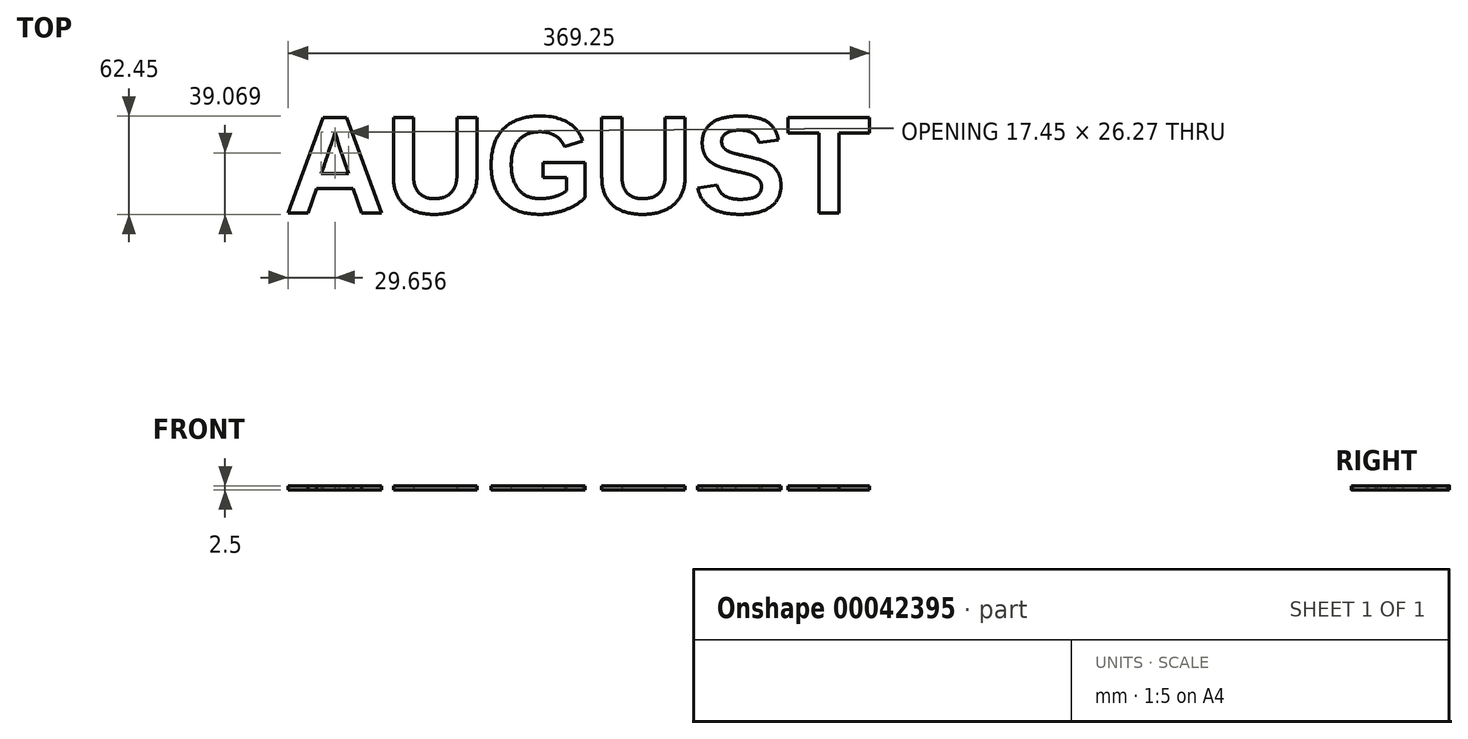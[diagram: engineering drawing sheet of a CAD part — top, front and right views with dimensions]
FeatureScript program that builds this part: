
annotation { "Feature Type Name" : "Feature", "Feature Type Description" : "" }
export const myFeature = defineFeature(function(context is Context, id is Id, definition is map)
    precondition{}
    {
        {
            assignVariable(context, id + "F0", {"name" : "x", "anyValue" : 2.5});
        }
        {
            var Q0;
            Q0=qCreatedBy(makeId("Top.planeOp"),FACE);
            var sketch = newSketch(context, id + "F1", { "sketchPlane" : qUnion([Q0])});
            skText(sketch, "E0", { "text": "AUGUST", "fontName": "Arimo-Bold.ttf"});
            skLineSegment(sketch, "E1.rect.bottom", {"start": v(222.25, -63.5) * mm, "end": v(-222.25, -63.5) * mm});
            skLineSegment(sketch, "E1.rect.top", {"start": v(222.25, 63.5) * mm, "end": v(-222.25, 63.5) * mm});
            skLineSegment(sketch, "E1.rect.left", {"start": v(222.25, -63.5) * mm, "end": v(222.25, 63.5) * mm});
            skLineSegment(sketch, "E1.rect.right", {"start": v(-222.25, -63.5) * mm, "end": v(-222.25, 63.5) * mm});
            skPoint(sketch, "E1.rect.middle", {"position": v(0, 0) * mm});
            const initialGuessF1  = {"E0": [-0.18572, -0.03175, 1, 0, 0.0635]};
            skSetInitialGuess(sketch, initialGuessF1);
            skSolve(sketch);
        }
        {
            var Q0;
            Q0=makeQuery(id+"F1.imprint","IMPRINT",FACE,{"disambiguationData":[TD([[makeQuery(id+"F1.imprint","IMPRINT",EDGE,{"derivedFrom":sQuery(id+"F1.wireOp",EDGE,"E0.sketch_text.stroke-0")}),-1.0]])]});
            var Q1;
            Q1=makeQuery(id+"F1.imprint","IMPRINT",FACE,{"disambiguationData":[TD([[makeQuery(id+"F1.imprint","IMPRINT",EDGE,{"derivedFrom":sQuery(id+"F1.wireOp",EDGE,"E0.sketch_text.stroke-15")}),-1.0]])]});
            var Q2;
            Q2=makeQuery(id+"F1.imprint","IMPRINT",FACE,{"disambiguationData":[TD([[makeQuery(id+"F1.imprint","IMPRINT",EDGE,{"derivedFrom":sQuery(id+"F1.wireOp",EDGE,"E0.sketch_text.stroke-29")}),-1.0]])]});
            var Q3;
            Q3=makeQuery(id+"F1.imprint","IMPRINT",FACE,{"disambiguationData":[TD([[makeQuery(id+"F1.imprint","IMPRINT",EDGE,{"derivedFrom":sQuery(id+"F1.wireOp",EDGE,"E0.sketch_text.stroke-50")}),-1.0]])]});
            var Q4;
            Q4=makeQuery(id+"F1.imprint","IMPRINT",FACE,{"disambiguationData":[TD([[makeQuery(id+"F1.imprint","IMPRINT",EDGE,{"derivedFrom":sQuery(id+"F1.wireOp",EDGE,"E0.sketch_text.stroke-64")}),-1.0]])]});
            var Q5;
            Q5=makeQuery(id+"F1.imprint","IMPRINT",FACE,{"disambiguationData":[TD([[makeQuery(id+"F1.imprint","IMPRINT",EDGE,{"derivedFrom":sQuery(id+"F1.wireOp",EDGE,"E0.sketch_text.stroke-95")}),-1.0]])]});
            extrude(context, id + "F2", {"entities" : qUnion([Q0, Q1, Q2, Q3, Q4, Q5]), "depth" : (getVariable(context, 'x')) * mm, "symmetric" : true});
        }
    });
